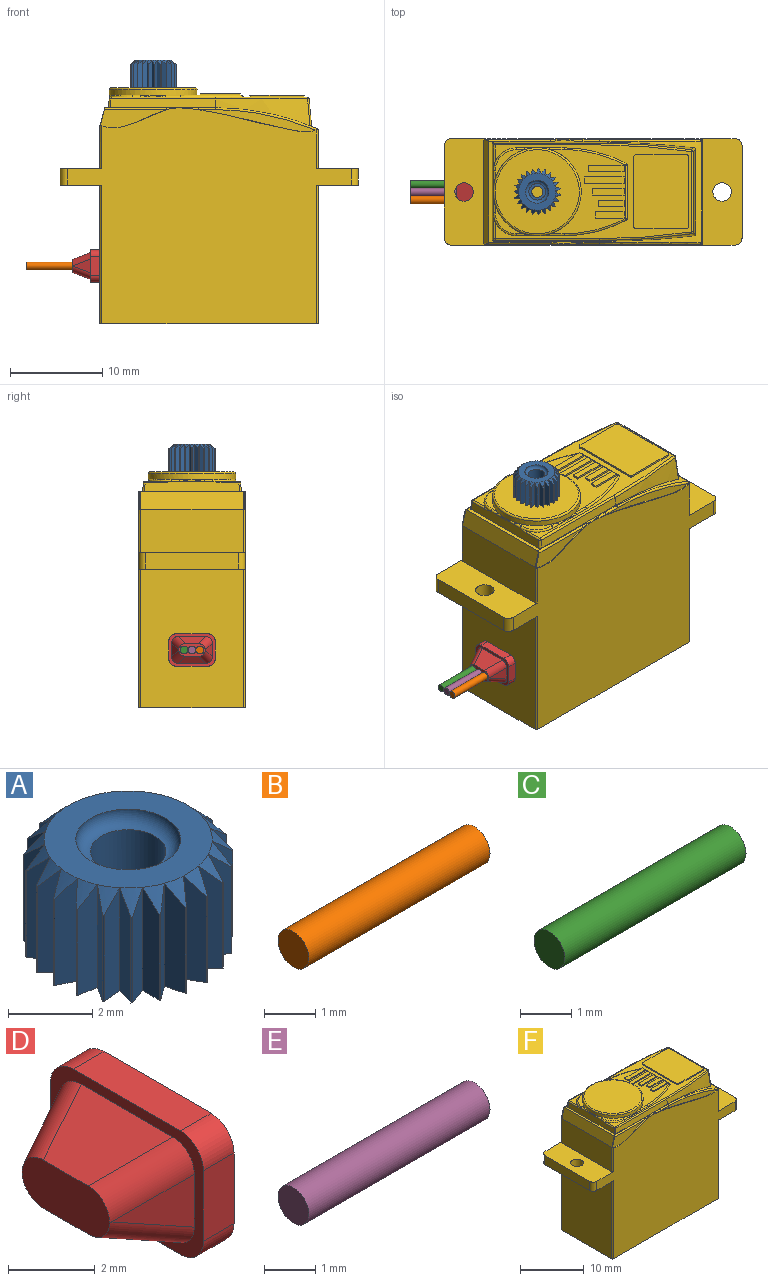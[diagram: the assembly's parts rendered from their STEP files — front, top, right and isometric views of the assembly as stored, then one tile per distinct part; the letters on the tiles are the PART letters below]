
ASSEMBLY  parts=6 mates=5
PART A: 98 faces, bbox 5x5x3.2 mm
  f0: cylinder r=2.5mm len=2.5mm, axis (0,0,-1), area 0.1mm2, adj f22,f46,f95,f96
  f1: cylinder r=2.5mm len=2.5mm, axis (0,0,-1), area 0.1mm2, adj f23,f46,f53,f97
  f2: cylinder r=2.5mm len=2.5mm, axis (0,0,-1), area 0.1mm2, adj f24,f46,f93,f94
  f3: cylinder r=2.5mm len=2.5mm, axis (0,0,-1), area 0.1mm2, adj f25,f46,f91,f92
  f4: cylinder r=2.5mm len=2.5mm, axis (0,0,-1), area 0.1mm2, adj f26,f46,f89,f90
  f5: cylinder r=2.5mm len=2.5mm, axis (0,0,-1), area 0.1mm2, adj f27,f46,f87,f88
  f6: cylinder r=2.5mm len=2.5mm, axis (0,0,-1), area 0.1mm2, adj f28,f46,f85,f86
  f7: cylinder r=2.5mm len=2.5mm, axis (0,0,-1), area 0.1mm2, adj f29,f46,f83,f84
  f8: cylinder r=2.5mm len=2.5mm, axis (0,0,-1), area 0.1mm2, adj f30,f46,f81,f82
  f9: cylinder r=2.5mm len=2.5mm, axis (0,0,-1), area 0.1mm2, adj f31,f46,f79,f80
  f10: cylinder r=2.5mm len=2.5mm, axis (0,0,-1), area 0.1mm2, adj f32,f46,f77,f78
  f11: cylinder r=2.5mm len=2.5mm, axis (0,0,-1), area 0.1mm2, adj f33,f46,f75,f76
  f12: cylinder r=2.5mm len=2.5mm, axis (0,0,-1), area 0.1mm2, adj f34,f46,f73,f74
  f13: cylinder r=2.5mm len=2.5mm, axis (0,0,-1), area 0.1mm2, adj f35,f46,f71,f72
  f14: cylinder r=2.5mm len=2.5mm, axis (0,0,-1), area 0.1mm2, adj f36,f46,f69,f70
  f15: cylinder r=2.5mm len=2.5mm, axis (0,0,-1), area 0.1mm2, adj f37,f46,f67,f68
  f16: cylinder r=2.5mm len=2.5mm, axis (0,0,-1), area 0.1mm2, adj f38,f46,f65,f66
  f17: cylinder r=2.5mm len=2.5mm, axis (0,0,-1), area 0.1mm2, adj f39,f46,f63,f64
  f18: cylinder r=2.5mm len=2.5mm, axis (0,0,-1), area 0.1mm2, adj f40,f46,f61,f62
  f19: cylinder r=2.5mm len=2.5mm, axis (0,0,-1), area 0.1mm2, adj f41,f46,f59,f60
  f20: cylinder r=2.5mm len=2.5mm, axis (0,0,-1), area 0.1mm2, adj f42,f46,f57,f58
  f21: cylinder r=2.5mm len=2.5mm, axis (0,0,-1), area 0.1mm2, adj f43,f46,f55,f56
  f22: cone r=2mm half-angle=45deg, axis (0,0,-1), area 0.2mm2, adj f0,f45,f95,f96
  f23: cone r=2mm half-angle=45deg, axis (0,0,-1), area 0.2mm2, adj f1,f45,f53,f97
  f24: cone r=2mm half-angle=45deg, axis (0,0,-1), area 0.2mm2, adj f2,f45,f93,f94
  f25: cone r=2mm half-angle=45deg, axis (0,0,-1), area 0.2mm2, adj f3,f45,f91,f92
  f26: cone r=2mm half-angle=45deg, axis (0,0,-1), area 0.2mm2, adj f4,f45,f89,f90
  f27: cone r=2mm half-angle=45deg, axis (0,0,-1), area 0.2mm2, adj f5,f45,f87,f88
  f28: cone r=2mm half-angle=45deg, axis (0,0,-1), area 0.2mm2, adj f6,f45,f85,f86
  f29: cone r=2mm half-angle=45deg, axis (0,0,-1), area 0.2mm2, adj f7,f45,f83,f84
  f30: cone r=2mm half-angle=45deg, axis (0,0,-1), area 0.2mm2, adj f8,f45,f81,f82
  f31: cone r=2mm half-angle=45deg, axis (0,0,-1), area 0.2mm2, adj f9,f45,f79,f80
  f32: cone r=2mm half-angle=45deg, axis (0,0,-1), area 0.2mm2, adj f10,f45,f77,f78
  f33: cone r=2mm half-angle=45deg, axis (0,0,-1), area 0.2mm2, adj f11,f45,f75,f76
  f34: cone r=2mm half-angle=45deg, axis (0,0,-1), area 0.2mm2, adj f12,f45,f73,f74
  f35: cone r=2mm half-angle=45deg, axis (0,0,-1), area 0.2mm2, adj f13,f45,f71,f72
  f36: cone r=2mm half-angle=45deg, axis (0,0,-1), area 0.2mm2, adj f14,f45,f69,f70
  f37: cone r=2mm half-angle=45deg, axis (0,0,-1), area 0.2mm2, adj f15,f45,f67,f68
  f38: cone r=2mm half-angle=45deg, axis (0,0,-1), area 0.2mm2, adj f16,f45,f65,f66
  f39: cone r=2mm half-angle=45deg, axis (0,0,-1), area 0.2mm2, adj f17,f45,f63,f64
  f40: cone r=2mm half-angle=45deg, axis (0,0,-1), area 0.2mm2, adj f18,f45,f61,f62
  f41: cone r=2mm half-angle=45deg, axis (0,0,-1), area 0.2mm2, adj f19,f45,f59,f60
  f42: cone r=2mm half-angle=45deg, axis (0,0,-1), area 0.2mm2, adj f20,f45,f57,f58
  f43: cone r=2mm half-angle=45deg, axis (0,0,-1), area 0.2mm2, adj f21,f45,f55,f56
  f44: cylinder r=0.9mm len=2.45mm, axis (0,0,-1), area 13.9mm2, adj f48,f51
  f45: plane 4x4mm, normal (0,0,1), area 7.7mm2, adj f22,f23,f24,f25,f26,f27,f28,f29
  f46: plane 4.99x4.98mm, normal (0,0,-1), area 14.8mm2, adj f0,f1,f2,f3,f4,f5,f6,f7
  f47: cylinder r=2.5mm len=2.5mm, axis (0,0,-1), area 0.1mm2, adj f46,f50,f52,f54
  f48: plane 1.8x1.8mm, normal (0,0,1), area 1.4mm2, adj f44,f49
  f49: cylinder r=0.6mm len=1.2mm, axis (0,0,-1), area 0.8mm2, adj f46,f48
  f50: cone r=2mm half-angle=45deg, axis (0,0,-1), area 0.2mm2, adj f45,f47,f52,f54
  f51: torus R=0.9mm, axis (0,0,1), area 3.9mm2, adj f44,f45
  f52: plane 3x0.48mm, normal (0.56,-0.83,0), area 1.6mm2, adj f46,f47,f50,f53
  f53: plane 3x0.48mm, normal (0.56,0.83,0), area 1.6mm2, adj f1,f23,f46,f52
  f54: plane 3x0.55mm, normal (0.31,0.95,0), area 1.6mm2, adj f46,f47,f50,f55
  f55: plane 3x0.44mm, normal (0.76,-0.65,0), area 1.6mm2, adj f21,f43,f46,f54
  f56: plane 3x0.58mm, normal (0.04,1,0), area 1.6mm2, adj f21,f43,f46,f57
  f57: plane 3x0.52mm, normal (0.91,-0.42,0), area 1.6mm2, adj f20,f42,f46,f56
  f58: plane 3x0.56mm, normal (-0.23,0.97,0), area 1.6mm2, adj f20,f42,f46,f59
  f59: plane 3x0.57mm, normal (0.99,-0.16,0), area 1.6mm2, adj f19,f41,f46,f58
  f60: plane 3x0.51mm, normal (-0.48,0.88,0), area 1.6mm2, adj f19,f41,f46,f61
  f61: plane 3x0.57mm, normal (0.99,0.11,0), area 1.6mm2, adj f18,f40,f46,f60
  f62: plane 3x0.41mm, normal (-0.7,0.71,0), area 1.6mm2, adj f18,f40,f46,f63
  f63: plane 3x0.54mm, normal (0.93,0.38,0), area 1.6mm2, adj f17,f39,f46,f62
  f64: plane 3x0.5mm, normal (-0.87,0.5,0), area 1.6mm2, adj f17,f39,f46,f65
  f65: plane 3x0.46mm, normal (0.79,0.61,0), area 1.6mm2, adj f16,f38,f46,f64
  f66: plane 3x0.56mm, normal (-0.97,0.25,0), area 1.6mm2, adj f16,f38,f46,f67
  f67: plane 3x0.46mm, normal (0.6,0.8,0), area 1.6mm2, adj f15,f37,f46,f66
  f68: plane 3x0.58mm, normal (-1,-0.02,0), area 1.6mm2, adj f15,f37,f46,f69
  f69: plane 3x0.54mm, normal (0.36,0.93,0), area 1.6mm2, adj f14,f36,f46,f68
  f70: plane 3x0.55mm, normal (-0.96,-0.29,0), area 1.6mm2, adj f14,f36,f46,f71
  f71: plane 3x0.58mm, normal (0.09,1,0), area 1.6mm2, adj f13,f35,f46,f70
  f72: plane 3x0.49mm, normal (-0.84,-0.54,0), area 1.6mm2, adj f13,f35,f46,f73
  f73: plane 3x0.57mm, normal (-0.18,0.98,0), area 1.6mm2, adj f12,f34,f46,f72
  f74: plane 3x0.43mm, normal (-0.66,-0.75,0), area 1.6mm2, adj f12,f34,f46,f75
  f75: plane 3x0.52mm, normal (-0.44,0.9,0), area 1.6mm2, adj f11,f33,f46,f74
  f76: plane 3x0.52mm, normal (-0.44,-0.9,0), area 1.6mm2, adj f11,f33,f46,f77
  f77: plane 3x0.43mm, normal (-0.66,0.75,0), area 1.6mm2, adj f10,f32,f46,f76
  f78: plane 3x0.57mm, normal (-0.18,-0.98,0), area 1.6mm2, adj f10,f32,f46,f79
  f79: plane 3x0.49mm, normal (-0.84,0.54,0), area 1.6mm2, adj f9,f31,f46,f78
  f80: plane 3x0.58mm, normal (0.09,-1,0), area 1.6mm2, adj f9,f31,f46,f81
  f81: plane 3x0.55mm, normal (-0.96,0.29,0), area 1.6mm2, adj f8,f30,f46,f80
  f82: plane 3x0.54mm, normal (0.36,-0.93,0), area 1.6mm2, adj f8,f30,f46,f83
  f83: plane 3x0.58mm, normal (-1,0.02,0), area 1.6mm2, adj f7,f29,f46,f82
  f84: plane 3x0.46mm, normal (0.6,-0.8,0), area 1.6mm2, adj f7,f29,f46,f85
  f85: plane 3x0.56mm, normal (-0.97,-0.25,0), area 1.6mm2, adj f6,f28,f46,f84
  f86: plane 3x0.46mm, normal (0.79,-0.61,0), area 1.6mm2, adj f6,f28,f46,f87
  f87: plane 3x0.5mm, normal (-0.87,-0.5,0), area 1.6mm2, adj f5,f27,f46,f86
  f88: plane 3x0.54mm, normal (0.93,-0.38,0), area 1.6mm2, adj f5,f27,f46,f89
  f89: plane 3x0.41mm, normal (-0.7,-0.71,0), area 1.6mm2, adj f4,f26,f46,f88
  f90: plane 3x0.57mm, normal (0.99,-0.11,0), area 1.6mm2, adj f4,f26,f46,f91
  f91: plane 3x0.51mm, normal (-0.48,-0.88,0), area 1.6mm2, adj f3,f25,f46,f90
  f92: plane 3x0.57mm, normal (0.99,0.16,0), area 1.6mm2, adj f3,f25,f46,f93
  f93: plane 3x0.56mm, normal (-0.23,-0.97,0), area 1.6mm2, adj f2,f24,f46,f92
  f94: plane 3x0.52mm, normal (0.91,0.42,0), area 1.6mm2, adj f2,f24,f46,f95
  f95: plane 3x0.58mm, normal (0.04,-1,0), area 1.6mm2, adj f0,f22,f46,f94
  f96: plane 3x0.44mm, normal (0.76,0.65,0), area 1.6mm2, adj f0,f22,f46,f97
  f97: plane 3x0.55mm, normal (0.31,-0.95,0), area 1.6mm2, adj f1,f23,f46,f96
PART B: 3 faces, bbox 5x0.9x0.9 mm
  f0: cylinder r=0.42mm len=5mm, axis (1,0,0), area 13.4mm2, adj f1,f2
  f1: plane 0.85x0.85mm, normal (-1,0,0), area 0.6mm2, adj f0
  f2: plane 0.85x0.85mm, normal (1,0,0), area 0.6mm2, adj f0
PART C: 3 faces, bbox 5x0.9x0.9 mm
  f0: cylinder r=0.42mm len=5mm, axis (1,0,0), area 13.4mm2, adj f1,f2
  f1: plane 0.85x0.85mm, normal (-1,0,0), area 0.6mm2, adj f0
  f2: plane 0.85x0.85mm, normal (1,0,0), area 0.6mm2, adj f0
PART D: 19 faces, bbox 3.1x5x3.5 mm
  f0: plane 5x3.5mm, normal (-1,0,0), area 4.7mm2, adj f1,f2,f3,f4,f6,f7,f8,f9
  f1: plane 2x1mm, normal (0,1,0), area 2mm2, adj f0,f5,f17,f18
  f2: plane 3.5x1mm, normal (0,0,-1), area 3.5mm2, adj f0,f5,f15,f17
  f3: plane 2x1mm, normal (0,-1,0), area 2mm2, adj f0,f5,f15,f16
  f4: plane 3.5x1mm, normal (0,0,1), area 3.5mm2, adj f0,f5,f16,f18
  f5: plane 5x3.5mm, normal (1,0,0), area 17mm2, adj f1,f2,f3,f4,f15,f16,f17,f18
  f6: plane 3x2mm, normal (-0.36,0,-0.93), area 4.8mm2, adj f0,f10,f12,f14
  f7: plane 1.95x1.5mm, normal (-0.36,-0.93,0), area 1.6mm2, adj f0,f11,f12
  f8: plane 3x2mm, normal (-0.36,0,0.93), area 4.8mm2, adj f0,f10,f11,f13
  f9: plane 1.95x1.5mm, normal (-0.36,0.93,0), area 1.6mm2, adj f0,f13,f14
  f10: plane 2.86x1.36mm, normal (-1,0,0), area 3.5mm2, adj f6,f8,f11,f12,f13,f14
  f11: cylinder r=0.75mm len=2.18mm, axis (0.88,-0.34,0.34), area 2.5mm2, adj f0,f7,f8,f10,f12
  f12: cylinder r=0.75mm len=2.18mm, axis (0.88,-0.34,-0.34), area 2.5mm2, adj f0,f6,f7,f10,f11
  f13: cylinder r=0.75mm len=2.18mm, axis (0.88,0.34,0.34), area 2.5mm2, adj f0,f8,f9,f10,f14
  f14: cylinder r=0.75mm len=2.18mm, axis (0.88,0.34,-0.34), area 2.5mm2, adj f0,f6,f9,f10,f13
  f15: cylinder r=0.75mm len=1mm, axis (1,0,0), area 1.2mm2, adj f0,f2,f3,f5
  f16: cylinder r=0.75mm len=1mm, axis (1,0,0), area 1.2mm2, adj f0,f3,f4,f5
  f17: cylinder r=0.75mm len=1mm, axis (1,0,0), area 1.2mm2, adj f0,f1,f2,f5
  f18: cylinder r=0.75mm len=1mm, axis (1,0,0), area 1.2mm2, adj f0,f1,f4,f5
PART E: 3 faces, bbox 5x0.9x0.9 mm
  f0: cylinder r=0.42mm len=5mm, axis (1,0,0), area 13.4mm2, adj f1,f2
  f1: plane 0.85x0.85mm, normal (-1,0,0), area 0.6mm2, adj f0
  f2: plane 0.85x0.85mm, normal (1,0,0), area 0.6mm2, adj f0
PART F: 137 faces, bbox 32.3x11.6x25.6 mm
  f0: plane 11.5x4.5mm, normal (0,0,-1), area 46.1mm2, adj f4,f11,f18,f62,f126,f131,f132,f133
  f1: plane 11.5x4.5mm, normal (0,0,-1), area 46.1mm2, adj f4,f12,f18,f63,f127,f129,f130,f135
  f2: extruded ~10.98x10.9mm, area 13.6mm2, adj f3,f8,f19,f20,f21,f75,f78,f100
  f3: plane 12.01x11.31mm, normal (0,0,1), area 7.2mm2, adj f2,f15,f22,f23,f24,f73,f74,f79
  f4: plane 30.7x23.48mm, normal (0,1,0), area 525mm2, adj f0,f1,f5,f7,f13,f17,f70,f128
  f5: cylinder r=0.2mm len=4.7mm, axis (0,0,-1), area 1.5mm2, adj f4,f6,f16,f17,f70,f72
  f6: cylinder r=0.2mm len=1.88mm, axis (-0.26,0,-0.97), area 0.2mm2, adj f5,f15,f72,f118
  f7: cylinder r=0.2mm len=4.28mm, axis (0,0,1), area 1.3mm2, adj f4,f8,f13,f14,f70
  f8: cylinder r=0.2mm len=11.33mm, axis (0,1,0), area 2.6mm2, adj f2,f7,f14,f66,f67,f70,f76,f77
  f9: plane 9.1x8.19mm, normal (0,0,1), area 32.3mm2, adj f31,f37,f38,f39,f40,f42,f43,f44
  f10: plane 21.34x10.25mm, normal (0,0,1), area 37.1mm2, adj f26,f27,f32,f33,f34,f35,f82,f83
  f11: plane 10x1.75mm, normal (-1,0,0), area 17.5mm2, adj f0,f17,f133,f134
  f12: plane 10x1.75mm, normal (1,0,0), area 17.5mm2, adj f1,f13,f135,f136
  f13: plane 11.5x4.5mm, normal (0,0,1), area 46.1mm2, adj f4,f7,f12,f14,f18,f63,f66,f135
  f14: plane 11.1x4.17mm, normal (1,0,0), area 46.3mm2, adj f7,f8,f13,f66
  f15: plane 11.1x1.9mm, normal (-0.97,0,0.26), area 21.8mm2, adj f3,f6,f16,f65,f118,f120
  f16: plane 11.1x4.7mm, normal (-1,0,0), area 52.2mm2, adj f5,f15,f17,f64
  f17: plane 11.5x4.5mm, normal (0,0,1), area 46.1mm2, adj f4,f5,f11,f16,f18,f62,f64,f133
  f18: plane 30.7x23.48mm, normal (0,-1,0), area 525mm2, adj f0,f1,f13,f17,f64,f66,f67,f128
  f19: bspline ~10.5x3.4mm, area 16.2mm2, adj f2,f24,f103,f106
  f20: plane 9.13x2.97mm, normal (1,0,0.09), area 26.6mm2, adj f2,f100,f103,f104
  f21: bspline ~10.5x3.4mm, area 16.2mm2, adj f2,f22,f100,f101
  f22: plane 11.39x0.97mm, normal (0,-1,0.09), area 11mm2, adj f3,f21,f96,f99
  f23: plane 10.44x1.29mm, normal (-1,0,0.09), area 10.9mm2, adj f3,f25,f92,f95,f96,f97,f107,f111
  f24: plane 11.39x0.97mm, normal (0,1,0.09), area 11mm2, adj f3,f19,f107,f108
  f25: plane 2.88x0.35mm, normal (-1,0,0), area 0.2mm2, adj f23,f90,f110
  f26: plane 2.88x0.35mm, normal (0,1,0), area 0.2mm2, adj f10,f85,f115
  f27: plane 2.88x0.35mm, normal (0,-1,0), area 0.2mm2, adj f10,f81,f91
  f28: plane 3.19x3.19mm, normal (0,0,1), area 2.2mm2, adj f31,f92,f93,f94
  f29: plane 3.19x3.19mm, normal (0,0,1), area 2.2mm2, adj f31,f112,f114,f116
  f30: plane 9.1x9.1mm, normal (0,0,1), area 65mm2, adj f121
  f31: cylinder r=4.75mm len=9.5mm, axis (0,0,1), area 17.9mm2, adj f9,f28,f29,f81,f85,f90,f91,f110
  f32: plane 7.6x0.2mm, normal (1,0,0), area 1.5mm2, adj f10,f36,f123,f124
  f33: plane 5.49x0.2mm, normal (0,-1,0), area 1.1mm2, adj f10,f36,f122,f123
  f34: plane 7.6x0.2mm, normal (-1,0,0), area 1.5mm2, adj f10,f36,f122,f125
  f35: plane 5.49x0.2mm, normal (0,1,0), area 1.1mm2, adj f10,f36,f124,f125
  f36: plane 8x5.89mm, normal (0,0,1), area 47.1mm2, adj f32,f33,f34,f35,f122,f123,f124,f125
  f37: plane 0.7x0.2mm, normal (1,0,0), area 0.1mm2, adj f9,f38,f40,f41
  f38: plane 3.13x0.2mm, normal (0,1,0), area 0.6mm2, adj f9,f37,f39,f41
  f39: plane 0.7x0.2mm, normal (-1,0,0), area 0.1mm2, adj f9,f38,f40,f41
  f40: plane 3.13x0.2mm, normal (0,-1,0), area 0.6mm2, adj f9,f37,f39,f41
  f41: plane 3.13x0.7mm, normal (0,0,1), area 2.2mm2, adj f37,f38,f39,f40
  f42: plane 0.7x0.2mm, normal (1,0,0), area 0.1mm2, adj f9,f43,f45,f46
  f43: plane 2.8x0.2mm, normal (0,1,0), area 0.6mm2, adj f9,f42,f44,f46
  f44: plane 0.7x0.2mm, normal (-1,0,0), area 0.1mm2, adj f9,f43,f45,f46
  f45: plane 2.8x0.2mm, normal (0,-1,0), area 0.6mm2, adj f9,f42,f44,f46
  f46: plane 2.8x0.7mm, normal (0,0,1), area 2mm2, adj f42,f43,f44,f45
  f47: plane 0.7x0.2mm, normal (1,0,0), area 0.1mm2, adj f9,f48,f50,f51
  f48: plane 3.43x0.2mm, normal (0,1,0), area 0.7mm2, adj f9,f47,f49,f51
  f49: plane 0.7x0.2mm, normal (-1,0,0), area 0.1mm2, adj f9,f48,f50,f51
  f50: plane 3.43x0.2mm, normal (0,-1,0), area 0.7mm2, adj f9,f47,f49,f51
  f51: plane 3.43x0.7mm, normal (0,0,1), area 2.4mm2, adj f47,f48,f49,f50
  f52: plane 0.7x0.2mm, normal (1,0,0), area 0.1mm2, adj f9,f53,f55,f56
  f53: plane 4.3x0.2mm, normal (0,1,0), area 0.9mm2, adj f9,f52,f54,f56
  f54: plane 0.7x0.2mm, normal (-1,0,0), area 0.1mm2, adj f9,f53,f55,f56
  f55: plane 4.3x0.2mm, normal (0,-1,0), area 0.9mm2, adj f9,f52,f54,f56
  f56: plane 4.3x0.7mm, normal (0,0,1), area 3mm2, adj f52,f53,f54,f55
  f57: plane 0.7x0.2mm, normal (1,0,0), area 0.1mm2, adj f9,f58,f60,f61
  f58: plane 3.84x0.2mm, normal (0,1,0), area 0.8mm2, adj f9,f57,f59,f61
  f59: plane 0.7x0.2mm, normal (-1,0,0), area 0.1mm2, adj f9,f58,f60,f61
  f60: plane 3.84x0.2mm, normal (0,-1,0), area 0.8mm2, adj f9,f57,f59,f61
  f61: plane 3.84x0.7mm, normal (0,0,1), area 2.7mm2, adj f57,f58,f59,f60
  f62: cylinder r=1mm len=2mm, axis (0,0,1), area 11mm2, adj f0,f17
  f63: cylinder r=1mm len=2mm, axis (0,0,1), area 11mm2, adj f1,f13
  f64: cylinder r=0.2mm len=4.7mm, axis (0,0,1), area 1.5mm2, adj f16,f17,f18,f65,f67,f69
  f65: cylinder r=0.2mm len=1.88mm, axis (0.26,0,0.97), area 0.2mm2, adj f15,f64,f69,f120
  f66: cylinder r=0.2mm len=4.28mm, axis (0,0,-1), area 1.3mm2, adj f8,f13,f14,f18,f67
  f67: extruded ~23.54x2.56mm, area 2.4mm2, adj f8,f18,f64,f66,f68,f69,f77,f78
  f68: plane 12.88x2.6mm, normal (0,-1,0), area 8.9mm2, adj f67,f78,f79
  f69: plane 7.48x2.5mm, normal (0,-1,0), area 8.7mm2, adj f64,f65,f67,f120
  f70: extruded ~23.54x2.56mm, area 2.4mm2, adj f4,f5,f7,f8,f71,f72,f73,f75
  f71: plane 12.88x2.6mm, normal (0,1,0), area 8.9mm2, adj f70,f74,f75
  f72: plane 7.48x2.5mm, normal (0,1,0), area 8.7mm2, adj f5,f6,f70,f118
  f73: bspline ~2.3x0.23mm, area 0.3mm2, adj f3,f70,f74
  f74: cylinder r=0.2mm len=1.8mm, axis (-1,0,0), area 0.6mm2, adj f3,f71,f73,f75
  f75: bspline ~13.87x2.82mm, area 3.5mm2, adj f2,f70,f71,f74,f76
  f76: sphere r=0.2mm, area 0mm2, adj f8,f70,f75
  f77: sphere r=0.2mm, area 0mm2, adj f8,f67,f78
  f78: bspline ~13.87x2.82mm, area 3.5mm2, adj f2,f67,f68,f77,f79
  f79: cylinder r=0.2mm len=1.8mm, axis (1,0,0), area 0.6mm2, adj f3,f68,f78,f80
  f80: bspline ~2.3x0.23mm, area 0.2mm2, adj f3,f67,f79
  f81: bspline ~1.46x0.23mm, area 0.1mm2, adj f27,f31,f82
  f82: cylinder r=0.2mm len=1.53mm, axis (-1,0,0), area 0.5mm2, adj f9,f10,f81,f83
  f83: bspline ~8.35x2.05mm, area 2.2mm2, adj f9,f10,f82,f84
  f84: sphere r=0.2mm, area 0mm2, adj f10,f83,f86
  f85: bspline ~1.36x0.2mm, area 0.1mm2, adj f26,f31,f87
  f86: cylinder r=0.2mm len=5.76mm, axis (0,-1,0), area 1.8mm2, adj f9,f10,f84,f88
  f87: cylinder r=0.2mm len=1.53mm, axis (1,0,0), area 0.5mm2, adj f9,f10,f85,f89
  f88: sphere r=0.2mm, area 0mm2, adj f10,f86,f89
  f89: bspline ~8.35x2.05mm, area 2.2mm2, adj f9,f10,f87,f88
  f90: bspline ~1.46x0.23mm, area 0.1mm2, adj f25,f31,f92
  f91: bspline ~1.36x0.2mm, area 0.1mm2, adj f27,f31,f93
  f92: cylinder r=0.2mm len=0.89mm, axis (0,1,0), area 0.3mm2, adj f23,f28,f90,f94
  f93: cylinder r=0.2mm len=0.89mm, axis (-1,0,0), area 0.3mm2, adj f10,f28,f91,f94
  f94: torus R=2.3mm, axis (0,0,-1), area 1.2mm2, adj f10,f28,f92,f93,f95
  f95: bspline ~0.94x0.2mm, area 0.1mm2, adj f23,f94,f97
  f96: cylinder r=0.2mm len=0.97mm, axis (0.09,0.09,0.99), area 0.3mm2, adj f3,f22,f23,f98
  f97: cylinder r=0.2mm len=1.88mm, axis (0,1,0), area 0.6mm2, adj f10,f23,f95,f98
  f98: sphere r=0.2mm, area 0mm2, adj f96,f97,f99
  f99: cylinder r=0.2mm len=11.31mm, axis (-1,0,0), area 3.4mm2, adj f10,f22,f98,f101
  f100: bspline ~2.98x0.43mm, area 0.8mm2, adj f2,f20,f21,f102
  f101: bspline ~13.69x1mm, area 3mm2, adj f10,f21,f99,f102
  f102: sphere r=0.2mm, area 0mm2, adj f100,f101,f104
  f103: bspline ~2.98x0.43mm, area 0.8mm2, adj f2,f19,f20,f105
  f104: cylinder r=0.2mm len=8.68mm, axis (0,-1,0), area 2.6mm2, adj f10,f20,f102,f105
  f105: sphere r=0.2mm, area 0mm2, adj f103,f104,f106
  f106: bspline ~13.69x1mm, area 3mm2, adj f10,f19,f105,f108
  f107: cylinder r=0.2mm len=0.97mm, axis (0.09,-0.09,0.99), area 0.3mm2, adj f3,f23,f24,f109
  f108: cylinder r=0.2mm len=11.31mm, axis (1,0,0), area 3.4mm2, adj f10,f24,f106,f109
  f109: sphere r=0.2mm, area 0mm2, adj f107,f108,f111
  f110: bspline ~1.46x0.23mm, area 0.1mm2, adj f25,f31,f112
  f111: cylinder r=0.2mm len=1.88mm, axis (0,1,0), area 0.6mm2, adj f10,f23,f109,f113
  f112: cylinder r=0.2mm len=0.89mm, axis (0,1,0), area 0.3mm2, adj f23,f29,f110,f114
  f113: bspline ~1.06x0.24mm, area 0.1mm2, adj f23,f111,f114
  f114: torus R=2.3mm, axis (0,0,-1), area 1.2mm2, adj f10,f29,f112,f113,f116
  f115: bspline ~1.46x0.23mm, area 0.1mm2, adj f26,f31,f116
  f116: cylinder r=0.2mm len=0.89mm, axis (1,0,0), area 0.3mm2, adj f10,f29,f114,f115
  f117: bspline ~1.53x0.24mm, area 0.1mm2, adj f3,f70,f118
  f118: cylinder r=0.2mm len=6.72mm, axis (-1,0,0), area 2.1mm2, adj f3,f6,f15,f72,f117
  f119: bspline ~1.39x0.2mm, area 0.1mm2, adj f3,f67,f120
  f120: cylinder r=0.2mm len=6.72mm, axis (1,0,0), area 2.1mm2, adj f3,f15,f65,f69,f119
  f121: torus R=4.55mm, axis (0,0,-1), area 9.2mm2, adj f30,f31
  f122: cylinder r=0.2mm len=0.2mm, axis (0,0,1), area 0.1mm2, adj f10,f33,f34,f36
  f123: cylinder r=0.2mm len=0.2mm, axis (0,0,1), area 0.1mm2, adj f10,f32,f33,f36
  f124: cylinder r=0.2mm len=0.2mm, axis (0,0,1), area 0.1mm2, adj f10,f32,f35,f36
  f125: cylinder r=0.2mm len=0.2mm, axis (0,0,1), area 0.1mm2, adj f10,f34,f35,f36
  f126: plane 15x11.1mm, normal (-1,0,0), area 166.5mm2, adj f0,f128,f131,f132
  f127: plane 15x11.1mm, normal (1,0,0), area 166.5mm2, adj f1,f128,f129,f130
  f128: plane 23.6x11.5mm, normal (0,0,-1), area 271.4mm2, adj f4,f18,f126,f127,f129,f130,f131,f132
  f129: cylinder r=0.2mm len=15mm, axis (0,0,1), area 4.7mm2, adj f1,f4,f127,f128
  f130: cylinder r=0.2mm len=15mm, axis (0,0,-1), area 4.7mm2, adj f1,f18,f127,f128
  f131: cylinder r=0.2mm len=15mm, axis (0,0,1), area 4.7mm2, adj f0,f4,f126,f128
  f132: cylinder r=0.2mm len=15mm, axis (0,0,-1), area 4.7mm2, adj f0,f18,f126,f128
  f133: cylinder r=0.75mm len=1.75mm, axis (0,0,1), area 2.1mm2, adj f0,f11,f17,f18
  f134: cylinder r=0.75mm len=1.75mm, axis (0,0,-1), area 2.1mm2, adj f0,f4,f11,f17
  f135: cylinder r=0.75mm len=1.75mm, axis (0,0,-1), area 2.1mm2, adj f1,f12,f13,f18
  f136: cylinder r=0.75mm len=1.75mm, axis (0,0,1), area 2.1mm2, adj f1,f4,f12,f13
PLACE A t=(-1.34,-1.96,-3.27)mm
PLACE B t=(-11.4,3.79,-13.77)mm
PLACE C t=(-11.4,3.79,-13.77)mm
PLACE D t=(-11.4,3.79,-13.77)mm
PLACE E t=(-11.4,3.79,-13.77)mm
PLACE F t=(-11.4,3.79,-13.77)mm
MATE fastened E.f0 <-> D.f10  axis (1,0,0) through (-10.1,-1.96,-22.52)mm
MATE fastened F.f31 <-> A.f0  axis (0,0,1) through (-1.34,-1.96,-3.27)mm
MATE fastened D.f5 <-> F.f126  axis (1,0,0) through (-7.1,-1.96,-22.52)mm
MATE fastened C.f0 <-> D.f10  axis (1,0,0) through (-10.1,-1.11,-22.52)mm
MATE fastened B.f0 <-> D.f10  axis (1,0,0) through (-10.1,-2.81,-22.52)mm
